# Revit family: SCST
name_source: partatom
category: Lighting Fixtures
units: mm (PartAtom-declared; Revit-internal decimal feet)

## family parameters
Cut with Voids When Loaded = No
Host = Face
Light Source = Yes
OmniClass Number = 23.80.70.11
OmniClass Title = Luminaries for Internal Lighting
Part Type = Normal
Room Calculation Point = No
Round Connector Dimension = Use Diameter
Shared = No

## types (1)
- SCST
    Apparent Load = 0 VA
    Backbox = White
    Color Filter = 16777215
    Default Elevation = 48"
    Description = LENSED STRIPLIGHT WITH SPECTRACLEAN™ ANTIMICROBIAL LIGHTING
    Dimming Lamp Color Temperature Shift = <None>
    Emit Shape Visible in Rendering = No
    Emit from Rectangle Length = 47 1/2"
    Emit from Rectangle Width = 4 1/4"
    Glass = White Glass
    Lamp = LED Lamp
    Manufacturer = Columbia Lighting
    Model = SCST
    Nominal Watts = 96 W
    Photometric Web File = generic.ies
    Row Length = 48"
    Tilt Angle = -90.00°
    URL = https://www.currentlighting.com
    Voltage = 120 V
    Warranty = 5 Year Limited Warranty
    Wattage Comments = Up to 110 lumens per watt

## geometry (parser evidence)
native form markers: Sweep x4
no freeform markers — native parametric forms only
